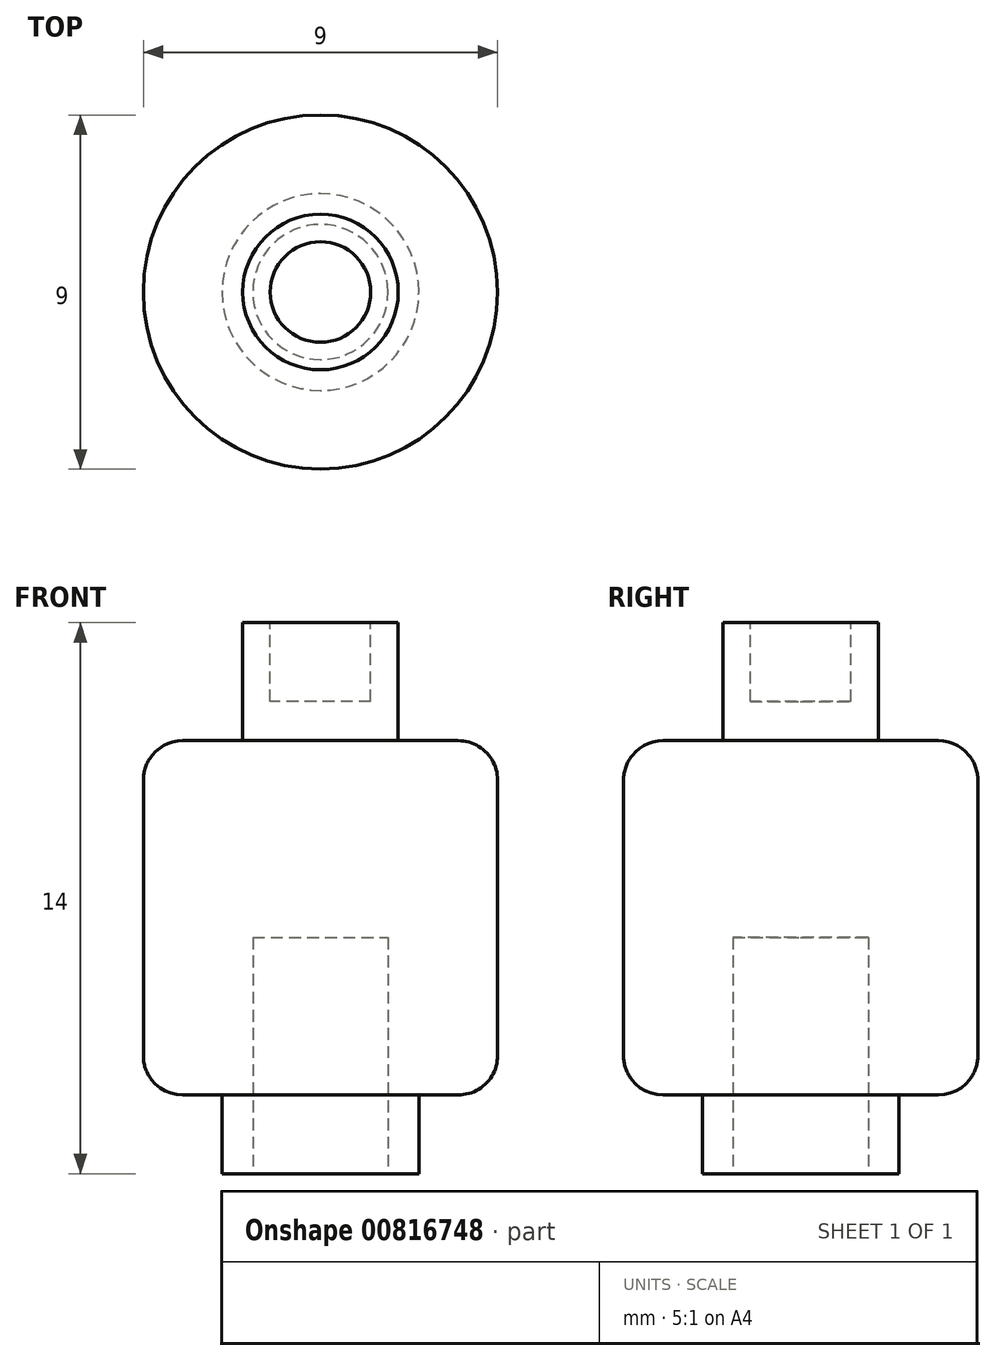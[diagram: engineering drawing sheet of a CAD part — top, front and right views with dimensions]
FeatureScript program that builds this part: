
annotation { "Feature Type Name" : "Feature", "Feature Type Description" : "" }
export const myFeature = defineFeature(function(context is Context, id is Id, definition is map)
    precondition{}
    {
        {
            var Q0;
            Q0=qCreatedBy(makeId("Top.planeOp"),FACE);
            var sketch = newSketch(context, id + "F0", { "sketchPlane" : qUnion([Q0])});
            skCircle(sketch, "E0", {"center": v(0, 0) * mm, "radius": 2.5 * mm});
            skSolve(sketch);
        }
        {
            var Q0;
            Q0=makeQuery(id+"F0.imprint","IMPRINT",FACE,{"disambiguationData":[TD([[makeQuery(id+"F0.imprint","IMPRINT",EDGE,{"derivedFrom":sQuery(id+"F0.wireOp",EDGE,"E0")}),1.0]])]});
            extrude(context, id + "F1", {"entities" : qUnion([Q0]), "depth" : 2 * mm, "offsetDistance" : 25 * mm});
        }
        {
            var Q0;
            Q0=makeQuery(id+"F1.opExtrude","CAP_FACE",FACE,{"disambiguationData":[OSD([sQuery(id+"F0.wireOp",EDGE,"E0")])],"isStart":false});
            var sketch = newSketch(context, id + "F2", { "sketchPlane" : qUnion([Q0])});
            skCircle(sketch, "E1", {"center": v(0, 0) * mm, "radius": 4.5 * mm});
            skSolve(sketch);
        }
        {
            var Q0;
            Q0 = qSketchRegion(id + "F2", true);
            extrude(context, id + "F3", {"entities" : qUnion([Q0]), "operationType" : NewBodyOperationType.ADD, "depth" : 9 * mm, "offsetDistance" : 25 * mm});
        }
        {
            var Q0;
            Q0=makeQuery(id+"F1.opExtrude","CAP_FACE",FACE,{"disambiguationData":[OSD([sQuery(id+"F0.wireOp",EDGE,"E0")])],"isStart":true});
            var sketch = newSketch(context, id + "F4", { "sketchPlane" : qUnion([Q0])});
            skCircle(sketch, "E2", {"center": v(0, 0) * mm, "radius": 1.72 * mm});
            skSolve(sketch);
        }
        {
            var Q0;
            Q0 = qSketchRegion(id + "F4", true);
            extrude(context, id + "F5", {"entities" : qUnion([Q0]), "operationType" : NewBodyOperationType.REMOVE, "oppositeDirection" : true, "depth" : 6 * mm, "offsetDistance" : 25 * mm});
        }
        {
            var Q0;
            Q0=makeQuery(id+"F3.opExtrude","CAP_EDGE",EDGE,{"disambiguationData":[OSD([sQuery(id+"F2.wireOp",EDGE,"E1")])],"isStart":false});
            var Q1;
            Q1=makeQuery(id+"F3.opExtrude","CAP_EDGE",EDGE,{"disambiguationData":[OSD([sQuery(id+"F2.wireOp",EDGE,"E1")])],"isStart":true});
            fillet(context, id + "F6", {"entities" : qUnion([Q0, Q1]), "radius" : 1 * mm, "tangentPropagation" : true, "allowEdgeOverflow" : false});
        }
        {
            var Q0;
            Q0=makeQuery(id+"F3.opExtrude","CAP_FACE",FACE,{"disambiguationData":[OSD([sQuery(id+"F2.wireOp",EDGE,"E1")])],"isStart":false});
            var sketch = newSketch(context, id + "F7", { "sketchPlane" : qUnion([Q0])});
            skCircle(sketch, "E3", {"center": v(0, 0) * mm, "radius": 1.98 * mm});
            skSolve(sketch);
        }
        {
            var Q0;
            Q0 = qSketchRegion(id + "F7", true);
            extrude(context, id + "F8", {"entities" : qUnion([Q0]), "operationType" : NewBodyOperationType.ADD, "depth" : 3 * mm, "offsetDistance" : 25 * mm});
        }
        {
            var Q0;
            Q0=makeQuery(id+"F8.opExtrude","CAP_FACE",FACE,{"disambiguationData":[OSD([sQuery(id+"F7.wireOp",EDGE,"E3")])],"isStart":false});
            var sketch = newSketch(context, id + "F9", { "sketchPlane" : qUnion([Q0])});
            skCircle(sketch, "E4", {"center": v(0, 0) * mm, "radius": 1.28 * mm});
            skSolve(sketch);
        }
        {
            var Q0;
            Q0 = qSketchRegion(id + "F9", true);
            extrude(context, id + "F10", {"entities" : qUnion([Q0]), "operationType" : NewBodyOperationType.REMOVE, "oppositeDirection" : true, "depth" : 2 * mm, "offsetDistance" : 25 * mm});
        }
    });
